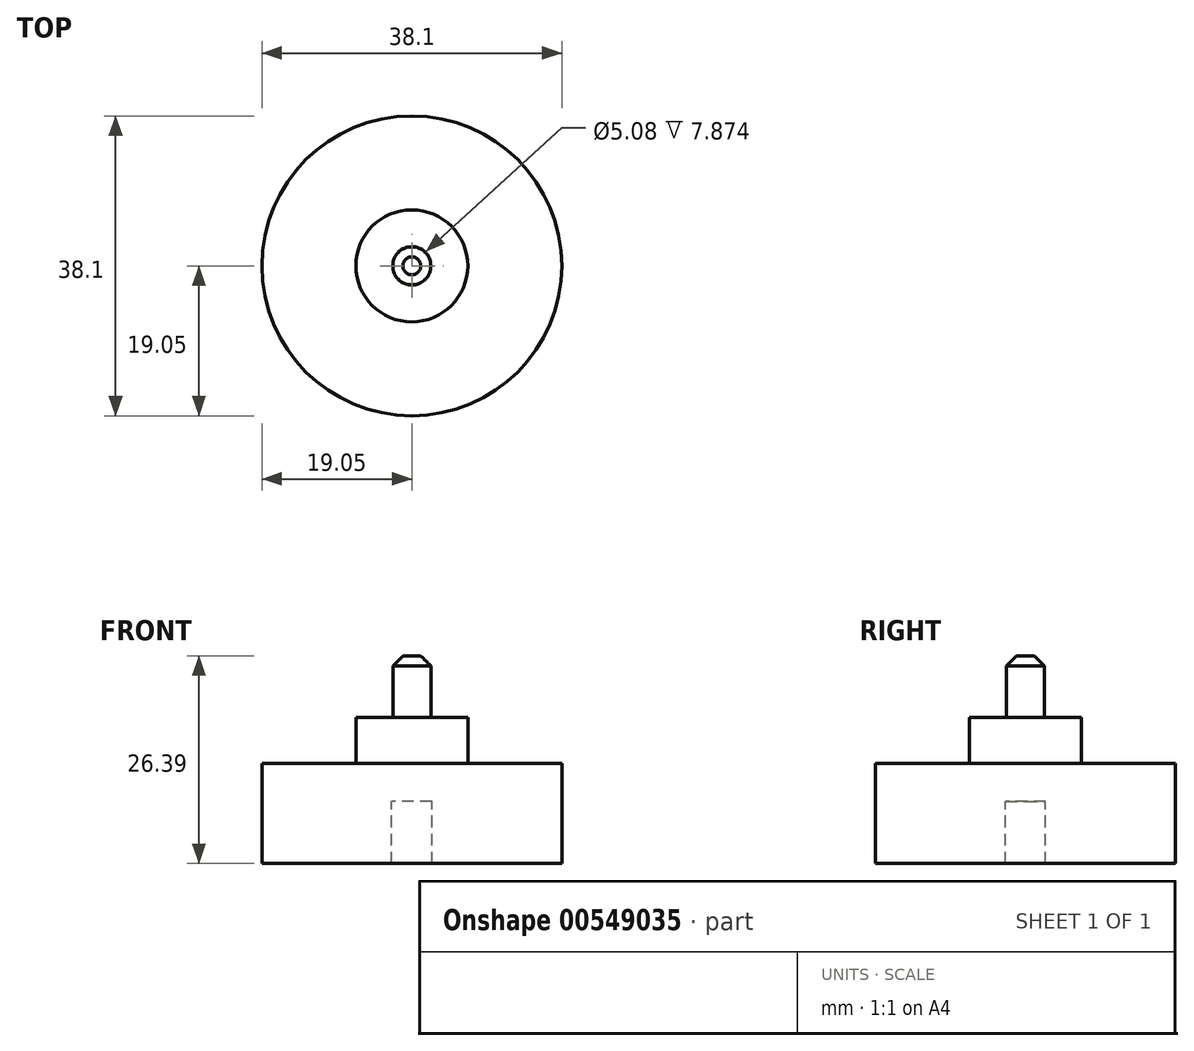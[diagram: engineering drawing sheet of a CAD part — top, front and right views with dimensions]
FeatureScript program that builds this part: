
annotation { "Feature Type Name" : "Feature", "Feature Type Description" : "" }
export const myFeature = defineFeature(function(context is Context, id is Id, definition is map)
    precondition{}
    {
        {
            var Q0;
            Q0=qCreatedBy(makeId("Front.planeOp"),FACE);
            var sketch = newSketch(context, id + "F0", { "sketchPlane" : qUnion([Q0])});
            skLineSegment(sketch, "E0", {"start": v(19.05, 0) * mm, "end": v(19.05, 12.7) * mm});
            skLineSegment(sketch, "E1", {"start": v(19.05, 12.7) * mm, "end": v(7.11, 12.7) * mm});
            skPoint(sketch, "E2.endSnap0", {"position": v(9.53, 12.7) * mm});
            skLineSegment(sketch, "E3", {"start": v(2.41, 18.54) * mm, "end": v(7.11, 18.54) * mm});
            skLineSegment(sketch, "E4", {"start": v(7.11, 18.54) * mm, "end": v(7.11, 12.7) * mm});
            skPoint(sketch, "E5.start.orphan", {"position": v(0, 12.7) * mm});
            skLineSegment(sketch, "E6", {"start": v(2.54, 0) * mm, "end": v(2.54, 7.87) * mm});
            skLineSegment(sketch, "E7", {"start": v(2.54, 7.87) * mm, "end": v(0, 7.87) * mm});
            skLineSegment(sketch, "E8", {"start": v(2.54, 0) * mm, "end": v(19.05, 0) * mm});
            skLineSegment(sketch, "E9", {"start": v(0, 26.4) * mm, "end": v(2.41, 26.4) * mm});
            skLineSegment(sketch, "E10", {"start": v(2.41, 26.4) * mm, "end": v(2.41, 18.54) * mm});
            skLineSegment(sketch, "E11", {"start": v(0, 26.4) * mm, "end": v(0, 7.87) * mm});
            skSolve(sketch);
        }
        {
            var Q0;
            Q0 = qSketchRegion(id + "F0", true);
            var Q1;
            Q1=sQuery(id+"F0.wireOp",EDGE,"E11");
            revolve(context, id + "F1", {"entities" : qUnion([Q0]), "axis" : qUnion([Q1]), "revolveType" : RevolveType.FULL});
        }
        {
            var Q0;
            Q0=makeQuery(id+"F1.opRevolve","SWEPT_EDGE",EDGE,{"disambiguationData":[OSD([sQuery(id+"F0.wireOp",EDGE,"E9"),sQuery(id+"F0.wireOp",EDGE,"E10")])]});
            chamfer(context, id + "F2", {"entities" : qUnion([Q0]), "width" : 1.27 * mm, "tangentPropagation" : true});
        }
    });
